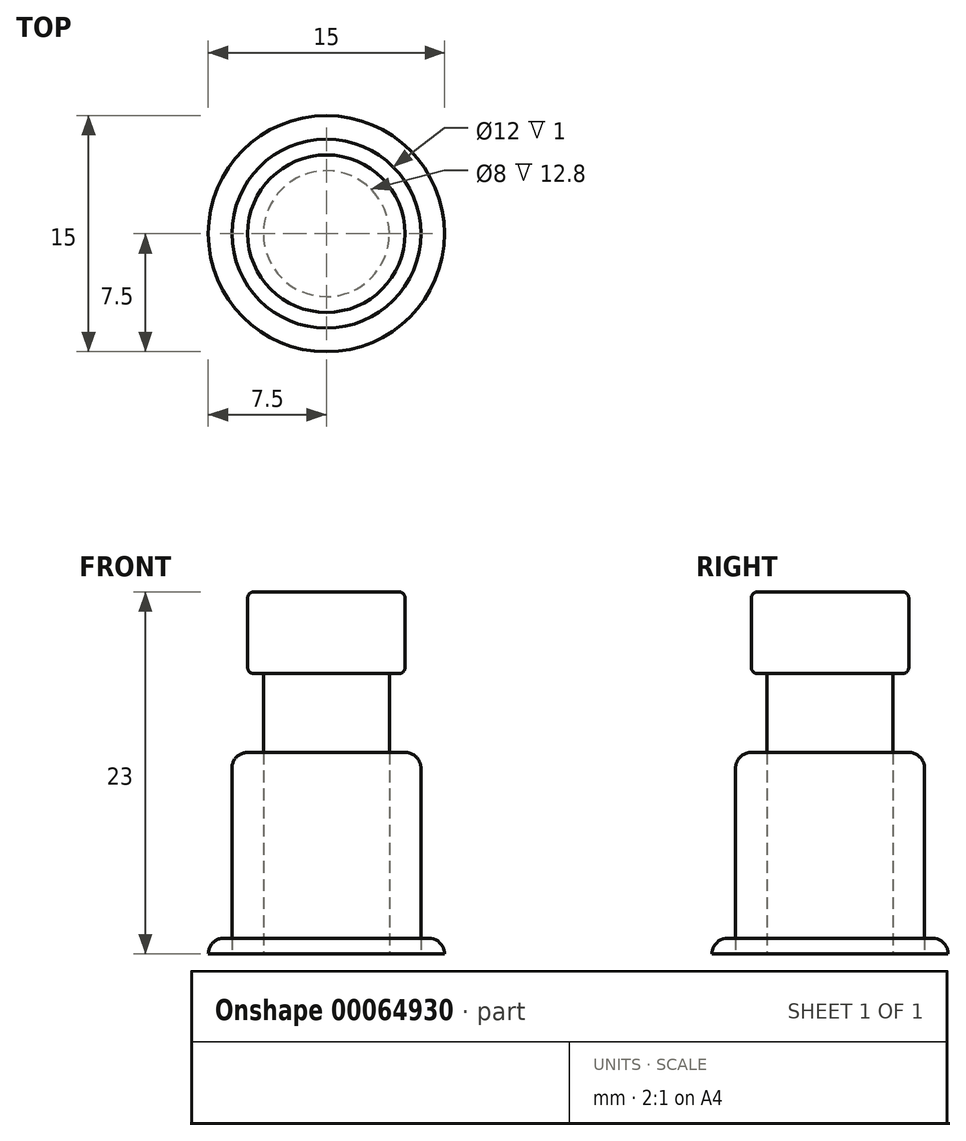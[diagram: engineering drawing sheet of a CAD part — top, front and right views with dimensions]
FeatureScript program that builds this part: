
annotation { "Feature Type Name" : "Feature", "Feature Type Description" : "" }
export const myFeature = defineFeature(function(context is Context, id is Id, definition is map)
    precondition{}
    {
        {
            var Q0;
            Q0=qCreatedBy(makeId("Top.planeOp"),FACE);
            var sketch = newSketch(context, id + "F0", { "sketchPlane" : qUnion([Q0])});
            skCircle(sketch, "E0", {"center": v(0, 0) * mm, "radius": 4 * mm});
            skSolve(sketch);
        }
        {
            var Q0;
            Q0=makeQuery(id+"F0.imprint","IMPRINT",FACE,{"disambiguationData":[TD([[makeQuery(id+"F0.imprint","IMPRINT",EDGE,{"derivedFrom":sQuery(id+"F0.wireOp",EDGE,"E0")}),1.0]])]});
            extrude(context, id + "F1", {"entities" : qUnion([Q0]), "depth" : 17.8 * mm});
        }
        {
            var Q0;
            Q0=makeQuery(id+"F1.opExtrude","CAP_FACE",FACE,{"disambiguationData":[OSD([sQuery(id+"F0.wireOp",EDGE,"E0")])],"isStart":false});
            var sketch = newSketch(context, id + "F2", { "sketchPlane" : qUnion([Q0])});
            skCircle(sketch, "E1", {"center": v(0, 0) * mm, "radius": 5 * mm});
            skSolve(sketch);
        }
        {
            var Q0;
            Q0=makeQuery(id+"F2.imprint","IMPRINT",FACE,{"disambiguationData":[TD([[makeQuery(id+"F2.imprint","IMPRINT",EDGE,{"derivedFrom":sQuery(id+"F2.wireOp",EDGE,"E1")}),1.0]])]});
            var Q1;
            Q1=makeQuery(id+"F2.imprint","IMPRINT",FACE,{"disambiguationData":[TD([[makeQuery(id+"F2.imprint","IMPRINT",EDGE,{"derivedFrom":makeQuery(id+"F1.opExtrude","CAP_EDGE",EDGE,{"disambiguationData":[OSD([sQuery(id+"F0.wireOp",EDGE,"E0")])],"isStart":false})}),1.0]])]});
            extrude(context, id + "F3", {"entities" : qUnion([Q0, Q1]), "operationType" : NewBodyOperationType.ADD, "depth" : 5.2 * mm});
        }
        {
            var Q0;
            Q0=makeQuery(id+"F3.opExtrude","CAP_EDGE",EDGE,{"disambiguationData":[OSD([sQuery(id+"F2.wireOp",EDGE,"E1")])],"isStart":false});
            var Q1;
            Q1=makeQuery(id+"F3.opExtrude","CAP_EDGE",EDGE,{"disambiguationData":[OSD([sQuery(id+"F2.wireOp",EDGE,"E1")])],"isStart":true});
            fillet(context, id + "F4", {"entities" : qUnion([Q0, Q1]), "radius" : .4 * mm, "tangentPropagation" : true, "allowEdgeOverflow" : false});
        }
        {
            var Q0;
            Q0=makeQuery(id+"F1.opExtrude","CAP_FACE",FACE,{"disambiguationData":[OSD([sQuery(id+"F0.wireOp",EDGE,"E0")])],"isStart":true});
            var sketch = newSketch(context, id + "F5", { "sketchPlane" : qUnion([Q0])});
            skCircle(sketch, "E2", {"center": v(0, 0) * mm, "radius": 6 * mm});
            skSolve(sketch);
        }
        {
            var Q0;
            Q0=makeQuery(id+"F5.imprint","IMPRINT",FACE,{"disambiguationData":[TD([[makeQuery(id+"F5.imprint","IMPRINT",EDGE,{"derivedFrom":sQuery(id+"F5.wireOp",EDGE,"E2")}),1.0]])]});
            extrude(context, id + "F6", {"entities" : qUnion([Q0]), "oppositeDirection" : true, "depth" : 12.8 * mm});
        }
        {
            var Q0;
            Q0=makeQuery(id+"F6.opExtrude","CAP_FACE",FACE,{"disambiguationData":[OSD([sQuery(id+"F0.wireOp",EDGE,"E0"),sQuery(id+"F5.wireOp",EDGE,"E2")])],"isStart":true});
            var sketch = newSketch(context, id + "F7", { "sketchPlane" : qUnion([Q0])});
            skCircle(sketch, "E3", {"center": v(0, 0) * mm, "radius": 7.5 * mm});
            skSolve(sketch);
        }
        {
            var Q0;
            Q0=makeQuery(id+"F7.imprint","IMPRINT",FACE,{"disambiguationData":[TD([[makeQuery(id+"F7.imprint","IMPRINT",EDGE,{"derivedFrom":sQuery(id+"F7.wireOp",EDGE,"E3")}),1.0]])]});
            extrude(context, id + "F8", {"entities" : qUnion([Q0]), "oppositeDirection" : true, "depth" : 1 * mm});
        }
        {
            var Q0;
            Q0=makeQuery(id+"F8.opExtrude","CAP_EDGE",EDGE,{"disambiguationData":[OSD([sQuery(id+"F7.wireOp",EDGE,"E3")])],"isStart":false});
            fillet(context, id + "F9", {"entities" : qUnion([Q0]), "radius" : 1 * mm, "tangentPropagation" : true, "allowEdgeOverflow" : false});
        }
        {
            var Q0;
            Q0=makeQuery(id+"F6.opExtrude","CAP_EDGE",EDGE,{"disambiguationData":[OSD([sQuery(id+"F5.wireOp",EDGE,"E2")])],"isStart":false});
            fillet(context, id + "F10", {"entities" : qUnion([Q0]), "radius" : 1 * mm, "allowEdgeOverflow" : false});
        }
    });
